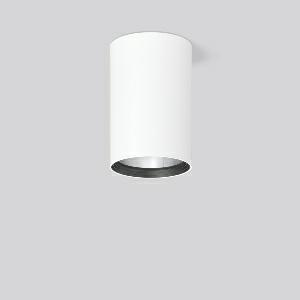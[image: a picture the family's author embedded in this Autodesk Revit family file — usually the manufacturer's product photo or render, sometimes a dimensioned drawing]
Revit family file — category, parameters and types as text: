
# Revit family: heledon_maxi_a_931238_002_76_cbb2
name_source: partatom
category: Lighting Fixtures
units: mm (PartAtom-declared; Revit-internal decimal feet)

## family parameters
Cut with Voids When Loaded = No
Host = Face
Light Source = No
Part Type = Normal
Room Calculation Point = No
Round Connector Dimension = Use Diameter
Shared = No

## types (1)
- HELEDON maxi A (1 x LED Modul 920 meat+, 2250 lm, 2000)
    Apparent Load = 33 VA
    Approval mark = CE
    CIE Flux Codes = 100 100 100 100 100
    Color Rendering = 90
    Color Temperature = 2000
    Default Elevation = 1800 mm
    Description = Series: HELEDON maxi
Cylindrical surface-mounted downlight. Housing: die-cast aluminium, powder-coated. Internal ceiling frame polycarbonate with bayonet mounting. Black plastic ring and recessed LED to prevent glare from the side. Optical assembly with reflector made of MIRO-Silver with 98% total light reflection for outstanding efficiency - can be changed without tools. Special LED for illumination of meat included. Suitable for Ceiling mounting. Easy installation with a separate ceiling frame with bayonet mounting and plug connection. Driver integrated. Connected via plug-in connector. High quality converter without flickering and stroboscopic effect. The following accessories can be mounted without use of tools: interchangeable lenses, decorative glasses, honeycomb louvre, clear and frosted diffusers, white interchangeable plastic ring. 
Colour: traffic white, matt (RAL 9016)
Diameter: 123 mm
Height: 183 mm
Lamp: LED
Socket: without socket
Colour temperature: meat +
System power: 33 W
Rated luminous flux: 2250 lm
Luminous efficiency: 68 lm/W
Control gear: Converter, dimmable, DALI
Protection class: I
Type of protection: IP 20
    Height = 183 mm
    Lamp = 1 x LED Modul 920 meat+
    Lamp Light Flux = 2250 lm
    Lamp count = 1
    Length = 123 mm
    Lifetime = 50000 h
    Luminous efficacy = 68 lm/W
    Manufacturer = RZB
    ModVariant = No
    Model = 931238.002.76
    Mounting Place = Ceiling
    Mounting Type = Surface mounted
    Number of Poles = 1
    OnlyDefault = Yes
    Power Factor = 1
    Product Name = HELEDON maxi A
    Product group = Surface mounted downlights
    ProductGroupID = 302
    Protection Class = Protection class I
    Protection Degree = IP 20
    RLX_Detail_Level = 1
    RLX_Emergency_Light_Flux = 0 lm
    RLX_Emergency_Type = 0
    RLX_Emergency_Type_DB = No
    RlxData = <blob elided: 98577 chars, md5=b04b3487>
    Socket = socket
    Standby Power = 0 W
    System Light Flux = 2250 lm
    System Power = 33 W
    Type Comments = Product without accessories
    Type Image = 931192.002.jpg
    URL = http://relux.com
    VarID = ---
    Voltage = 230 V
    Voltage Range = 220-240 V
    Weight = 0.00 kg
    Width = 0 mm  [stored 0 ft]

note: [stored X ft] marks values corroborated as IEEE doubles in the binary element streams (Revit-internal decimal feet)

## geometry (parser evidence)
native form markers: Blend x4, Sweep x11
no freeform markers — native parametric forms only
